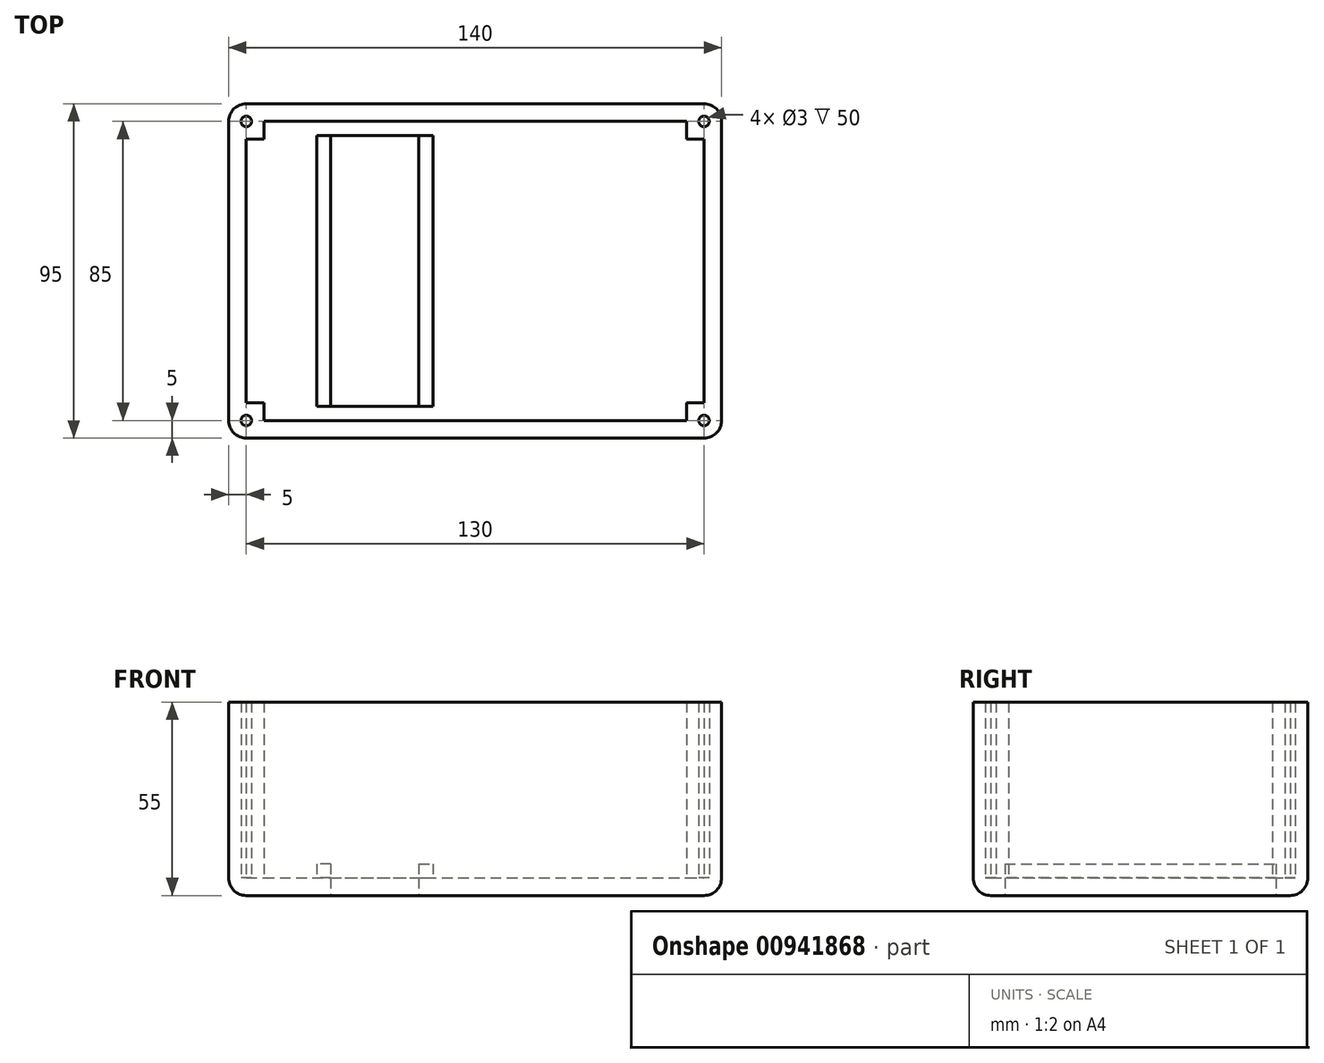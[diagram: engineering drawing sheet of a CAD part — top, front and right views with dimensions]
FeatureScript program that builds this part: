
annotation { "Feature Type Name" : "Feature", "Feature Type Description" : "" }
export const myFeature = defineFeature(function(context is Context, id is Id, definition is map)
    precondition{}
    {
        {
            var Q0;
            Q0=qCreatedBy(makeId("Top.planeOp"),FACE);
            var sketch = newSketch(context, id + "F0", { "sketchPlane" : qUnion([Q0])});
            skLineSegment(sketch, "E0.bottom", {"start": v(5, 0) * mm, "end": v(135, 0) * mm});
            skLineSegment(sketch, "E0.top", {"start": v(5, 95) * mm, "end": v(135, 95) * mm});
            skLineSegment(sketch, "E0.left", {"start": v(0, 5) * mm, "end": v(0, 90) * mm});
            skLineSegment(sketch, "E0.right", {"start": v(140, 5) * mm, "end": v(140, 90) * mm});
            skPoint(sketch, "E1.visualSharp", {"position": v(0, 95) * mm});
            skArc(sketch, "E1.filletArc", {"start": v(5, 95) * mm, "mid": v(1.46, 93.54) * mm, "end": v(0, 90) * mm});
            skPoint(sketch, "E2.visualSharp", {"position": v(0, 0) * mm});
            skArc(sketch, "E2.filletArc", {"start": v(0, 5) * mm, "mid": v(1.46, 1.46) * mm, "end": v(5, 0) * mm});
            skPoint(sketch, "E3.visualSharp", {"position": v(140, 0) * mm});
            skArc(sketch, "E3.filletArc", {"start": v(135, 0) * mm, "mid": v(138.54, 1.46) * mm, "end": v(140, 5) * mm});
            skPoint(sketch, "E4.visualSharp", {"position": v(140, 95) * mm});
            skArc(sketch, "E4.filletArc", {"start": v(140, 90) * mm, "mid": v(138.54, 93.54) * mm, "end": v(135, 95) * mm});
            skLineSegment(sketch, "E5.0", {"start": v(29, 9) * mm, "end": v(29, 86) * mm});
            skLineSegment(sketch, "E6.0", {"start": v(54, 9) * mm, "end": v(54, 86) * mm});
            skLineSegment(sketch, "E7.0", {"start": v(29, 86) * mm, "end": v(54, 86) * mm});
            skLineSegment(sketch, "E8.0", {"start": v(29, 9) * mm, "end": v(54, 9) * mm});
            skSolve(sketch);
        }
        {
            var Q0;
            Q0=makeQuery(id+"F0.imprint","IMPRINT",FACE,{"disambiguationData":[TD([[makeQuery(id+"F0.imprint","IMPRINT",EDGE,{"derivedFrom":sQuery(id+"F0.wireOp",EDGE,"E0.bottom")}),1.0]])]});
            extrude(context, id + "F1", {"entities" : qUnion([Q0]), "depth" : 5 * mm, "offsetDistance" : 25 * mm});
        }
        {
            var Q0;
            Q0=makeQuery(id+"F1.opExtrude","CAP_FACE",FACE,{"disambiguationData":[OSD([sQuery(id+"F0.wireOp",EDGE,"E0.bottom"),sQuery(id+"F0.wireOp",EDGE,"E0.top"),sQuery(id+"F0.wireOp",EDGE,"E0.left"),sQuery(id+"F0.wireOp",EDGE,"E0.right"),sQuery(id+"F0.wireOp",EDGE,"E1.filletArc"),sQuery(id+"F0.wireOp",EDGE,"E2.filletArc"),sQuery(id+"F0.wireOp",EDGE,"E3.filletArc"),sQuery(id+"F0.wireOp",EDGE,"E4.filletArc"),sQuery(id+"F0.wireOp",EDGE,"E5.0"),sQuery(id+"F0.wireOp",EDGE,"E6.0"),sQuery(id+"F0.wireOp",EDGE,"E7.0"),sQuery(id+"F0.wireOp",EDGE,"E8.0")])],"isStart":false});
            var sketch = newSketch(context, id + "F2", { "sketchPlane" : qUnion([Q0])});
            skLineSegment(sketch, "E9.bottom", {"start": v(5, 0) * mm, "end": v(135, 0) * mm});
            skLineSegment(sketch, "E9.top", {"start": v(5, 95) * mm, "end": v(135, 95) * mm});
            skLineSegment(sketch, "E9.left", {"start": v(0, 5) * mm, "end": v(0, 90) * mm});
            skLineSegment(sketch, "E9.right", {"start": v(140, 5) * mm, "end": v(140, 90) * mm});
            skPoint(sketch, "E10.visualSharp", {"position": v(0, 95) * mm});
            skArc(sketch, "E10.filletArc", {"start": v(5, 95) * mm, "mid": v(1.46, 93.54) * mm, "end": v(0, 90) * mm});
            skPoint(sketch, "E11.visualSharp", {"position": v(0, 0) * mm});
            skArc(sketch, "E11.filletArc", {"start": v(0, 5) * mm, "mid": v(1.46, 1.46) * mm, "end": v(5, 0) * mm});
            skPoint(sketch, "E12.visualSharp", {"position": v(140, 0) * mm});
            skArc(sketch, "E12.filletArc", {"start": v(135, 0) * mm, "mid": v(138.54, 1.46) * mm, "end": v(140, 5) * mm});
            skPoint(sketch, "E13.visualSharp", {"position": v(140, 95) * mm});
            skArc(sketch, "E13.filletArc", {"start": v(140, 90) * mm, "mid": v(138.54, 93.54) * mm, "end": v(135, 95) * mm});
            skLineSegment(sketch, "E14.0", {"start": v(5, 10) * mm, "end": v(5, 85) * mm});
            skLineSegment(sketch, "E14.1", {"start": v(10, 5) * mm, "end": v(130, 5) * mm});
            skLineSegment(sketch, "E14.2", {"start": v(135, 10) * mm, "end": v(135, 85) * mm});
            skLineSegment(sketch, "E14.3", {"start": v(10, 90) * mm, "end": v(130, 90) * mm});
            skLineSegment(sketch, "E15.0", {"start": v(10, 5) * mm, "end": v(10, 10) * mm});
            skLineSegment(sketch, "E16.0", {"start": v(5, 85) * mm, "end": v(10, 85) * mm});
            skLineSegment(sketch, "E17.0", {"start": v(130, 5) * mm, "end": v(130, 10) * mm});
            skLineSegment(sketch, "E18.0", {"start": v(5, 10) * mm, "end": v(10, 10) * mm});
            skLineSegment(sketch, "E19.trimOffspring", {"start": v(130, 85) * mm, "end": v(135, 85) * mm});
            skLineSegment(sketch, "E20.trimOffspring", {"start": v(10, 85) * mm, "end": v(10, 90) * mm});
            skLineSegment(sketch, "E21.trimOffspring", {"start": v(130, 10) * mm, "end": v(135, 10) * mm});
            skLineSegment(sketch, "E22.trimOffspring", {"start": v(130, 85) * mm, "end": v(130, 90) * mm});
            skCircle(sketch, "E23", {"center": v(5, 90) * mm, "radius": 1.5 * mm});
            skCircle(sketch, "E24", {"center": v(135, 90) * mm, "radius": 1.5 * mm});
            skCircle(sketch, "E25", {"center": v(135, 5) * mm, "radius": 1.5 * mm});
            skCircle(sketch, "E26", {"center": v(5, 5) * mm, "radius": 1.5 * mm});
            skSolve(sketch);
        }
        {
            var Q0;
            Q0=makeQuery(id+"F2.imprint","IMPRINT",FACE,{"disambiguationData":[TD([[makeQuery(id+"F2.imprint","IMPRINT",EDGE,{"derivedFrom":sQuery(id+"F2.wireOp",EDGE,"E9.bottom")}),1.0]])]});
            extrude(context, id + "F3", {"entities" : qUnion([Q0]), "operationType" : NewBodyOperationType.ADD, "depth" : 50 * mm, "offsetDistance" : 25 * mm});
        }
        {
            var Q0;
            Q0=makeQuery(id+"F1.opExtrude","CAP_EDGE",EDGE,{"disambiguationData":[OSD([sQuery(id+"F0.wireOp",EDGE,"E0.top")])],"isStart":true});
            fillet(context, id + "F4", {"entities" : qUnion([Q0]), "radius" : 5 * mm, "tangentPropagation" : true, "allowEdgeOverflow" : false});
        }
        {
            var Q0;
            {var subQ0=sQuery(id+"F0.wireOp",EDGE,"E5.0");var subQ1=sQuery(id+"F0.wireOp",EDGE,"E6.0");var subQ2=sQuery(id+"F0.wireOp",EDGE,"E7.0");var subQ3=sQuery(id+"F0.wireOp",EDGE,"E8.0");Q0=makeQuery(id+"F3.boolean.opBoolean","SPLIT",FACE,{"disambiguationData":[TD([makeQuery(id+"F1.opExtrude","SWEPT_FACE",FACE,{"disambiguationData":[OSD([subQ0])]})])],"derivedFrom":makeQuery(id+"F1.opExtrude","CAP_FACE",FACE,{"disambiguationData":[OSD([sQuery(id+"F0.wireOp",EDGE,"E0.bottom"),sQuery(id+"F0.wireOp",EDGE,"E0.top"),sQuery(id+"F0.wireOp",EDGE,"E0.left"),sQuery(id+"F0.wireOp",EDGE,"E0.right"),sQuery(id+"F0.wireOp",EDGE,"E1.filletArc"),sQuery(id+"F0.wireOp",EDGE,"E2.filletArc"),sQuery(id+"F0.wireOp",EDGE,"E3.filletArc"),sQuery(id+"F0.wireOp",EDGE,"E4.filletArc"),subQ0,subQ1,subQ2,subQ3])],"isStart":false})});}
            var sketch = newSketch(context, id + "F5", { "sketchPlane" : qUnion([Q0])});
            skLineSegment(sketch, "E27.bottom", {"start": v(54, 86) * mm, "end": v(58, 86) * mm});
            skLineSegment(sketch, "E27.top", {"start": v(54, 9) * mm, "end": v(58, 9) * mm});
            skLineSegment(sketch, "E27.left", {"start": v(54, 86) * mm, "end": v(54, 9) * mm});
            skLineSegment(sketch, "E27.right", {"start": v(58, 86) * mm, "end": v(58, 9) * mm});
            skLineSegment(sketch, "E28.bottom", {"start": v(29, 86) * mm, "end": v(25, 86) * mm});
            skLineSegment(sketch, "E28.top", {"start": v(29, 9) * mm, "end": v(25, 9) * mm});
            skLineSegment(sketch, "E28.left", {"start": v(29, 86) * mm, "end": v(29, 9) * mm});
            skLineSegment(sketch, "E28.right", {"start": v(25, 86) * mm, "end": v(25, 9) * mm});
            skSolve(sketch);
        }
        {
            var Q0;
            Q0=makeQuery(id+"F5.imprint","IMPRINT",FACE,{"disambiguationData":[TD([[makeQuery(id+"F5.imprint","IMPRINT",EDGE,{"derivedFrom":sQuery(id+"F5.wireOp",EDGE,"E28.bottom")}),1.0]])]});
            var Q1;
            Q1=makeQuery(id+"F5.imprint","IMPRINT",FACE,{"disambiguationData":[TD([[makeQuery(id+"F5.imprint","IMPRINT",EDGE,{"derivedFrom":sQuery(id+"F5.wireOp",EDGE,"E27.bottom")}),-1.0]])]});
            extrude(context, id + "F6", {"entities" : qUnion([Q0, Q1]), "operationType" : NewBodyOperationType.ADD, "depth" : 4 * mm, "offsetDistance" : 25 * mm});
        }
    });
